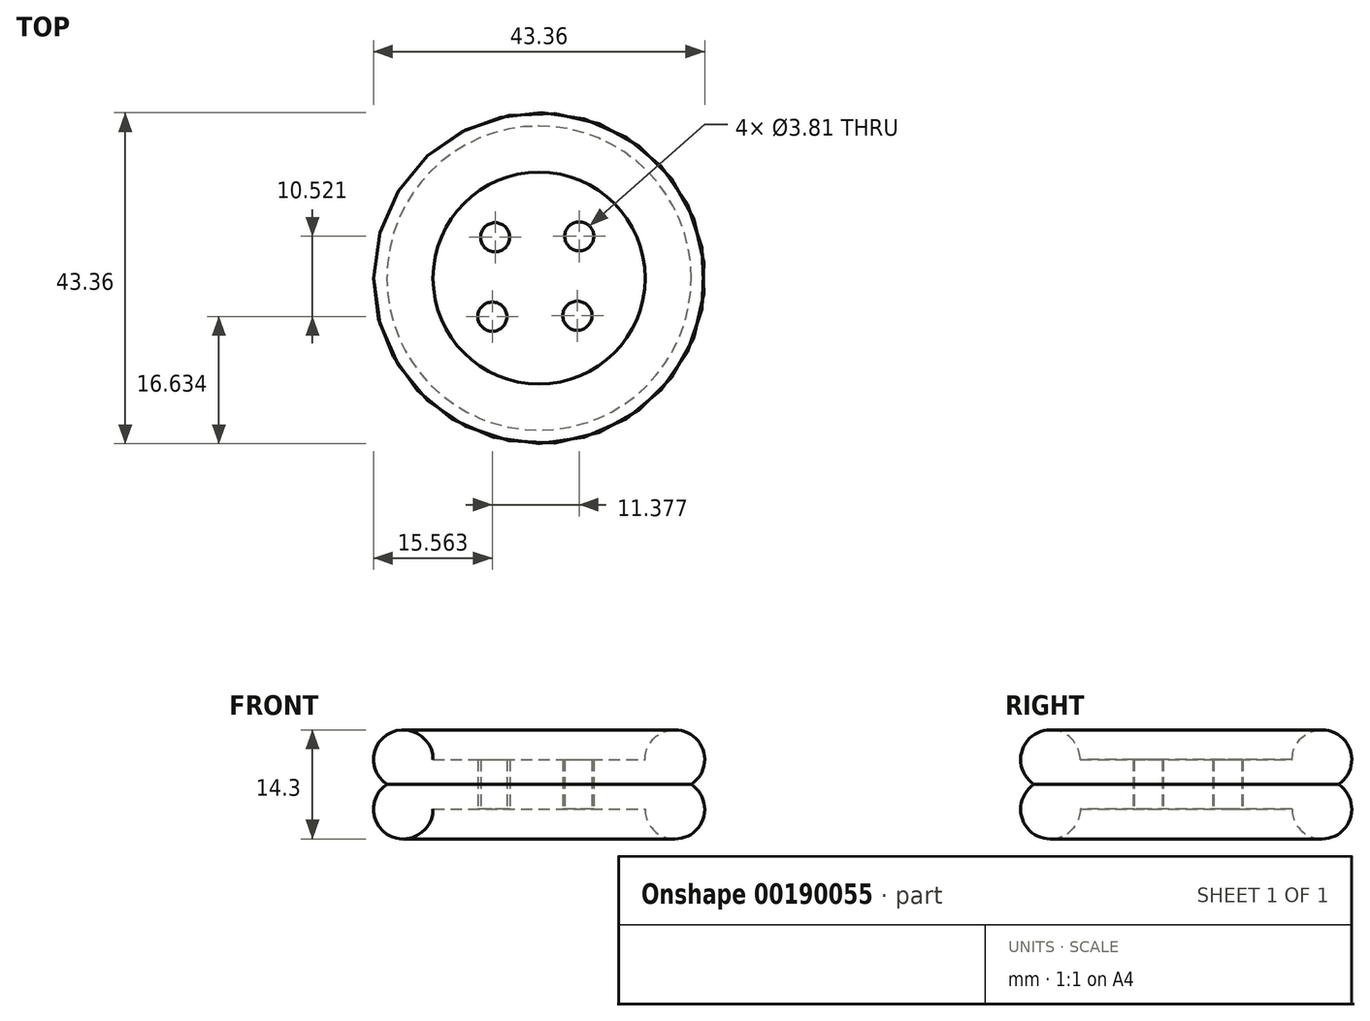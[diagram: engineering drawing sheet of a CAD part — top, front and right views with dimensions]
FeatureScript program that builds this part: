
annotation { "Feature Type Name" : "Feature", "Feature Type Description" : "" }
export const myFeature = defineFeature(function(context is Context, id is Id, definition is map)
    precondition{}
    {
        {
            var Q0;
            Q0=qCreatedBy(makeId("Front.planeOp"),FACE);
            var sketch = newSketch(context, id + "F0", { "sketchPlane" : qUnion([Q0])});
            skLineSegment(sketch, "E0.bottom", {"start": v(0, 0) * mm, "end": v(-17.78, 0) * mm});
            skLineSegment(sketch, "E0.top", {"start": v(0, 6.5) * mm, "end": v(-17.78, 6.5) * mm});
            skLineSegment(sketch, "E0.left", {"start": v(0, 0) * mm, "end": v(0, 6.5) * mm});
            skLineSegment(sketch, "E0.right", {"start": v(-17.78, 0) * mm, "end": v(-17.78, 6.5) * mm});
            skArc(sketch, "E1", {"start": v(-13.88, 6.5) * mm, "mid": v(-20.54, 9.26) * mm, "end": v(-17.78, 2.61) * mm});
            skArc(sketch, "E2", {"start": v(-17.78, 3.9) * mm, "mid": v(-20.54, -2.76) * mm, "end": v(-13.88, 0) * mm});
            skSolve(sketch);
        }
        {
            var Q0;
            Q0 = qSketchRegion(id + "F0", true);
            var Q1;
            Q1=sQuery(id+"F0.wireOp",EDGE,"E0.left");
            revolve(context, id + "F1", {"entities" : qUnion([Q0]), "axis" : qUnion([Q1]), "revolveType" : RevolveType.FULL});
        }
        {
            var Q0;
            Q0=qCreatedBy(makeId("Top.planeOp"),FACE);
            var sketch = newSketch(context, id + "F2", { "sketchPlane" : qUnion([Q0])});
            skCircle(sketch, "E3", {"center": v(-5.75, 5.35) * mm, "radius": 1.9 * mm});
            skCircle(sketch, "E4", {"center": v(5.26, 5.48) * mm, "radius": 1.9 * mm});
            skCircle(sketch, "E5", {"center": v(-6.12, -5.05) * mm, "radius": 1.9 * mm});
            skCircle(sketch, "E6", {"center": v(5.02, -4.92) * mm, "radius": 1.9 * mm});
            skSolve(sketch);
        }
        {
            var Q0;
            Q0 = qSketchRegion(id + "F2", true);
            extrude(context, id + "F3", {"entities" : qUnion([Q0]), "operationType" : NewBodyOperationType.REMOVE, "depth" : 25.4 * mm});
        }
    });
